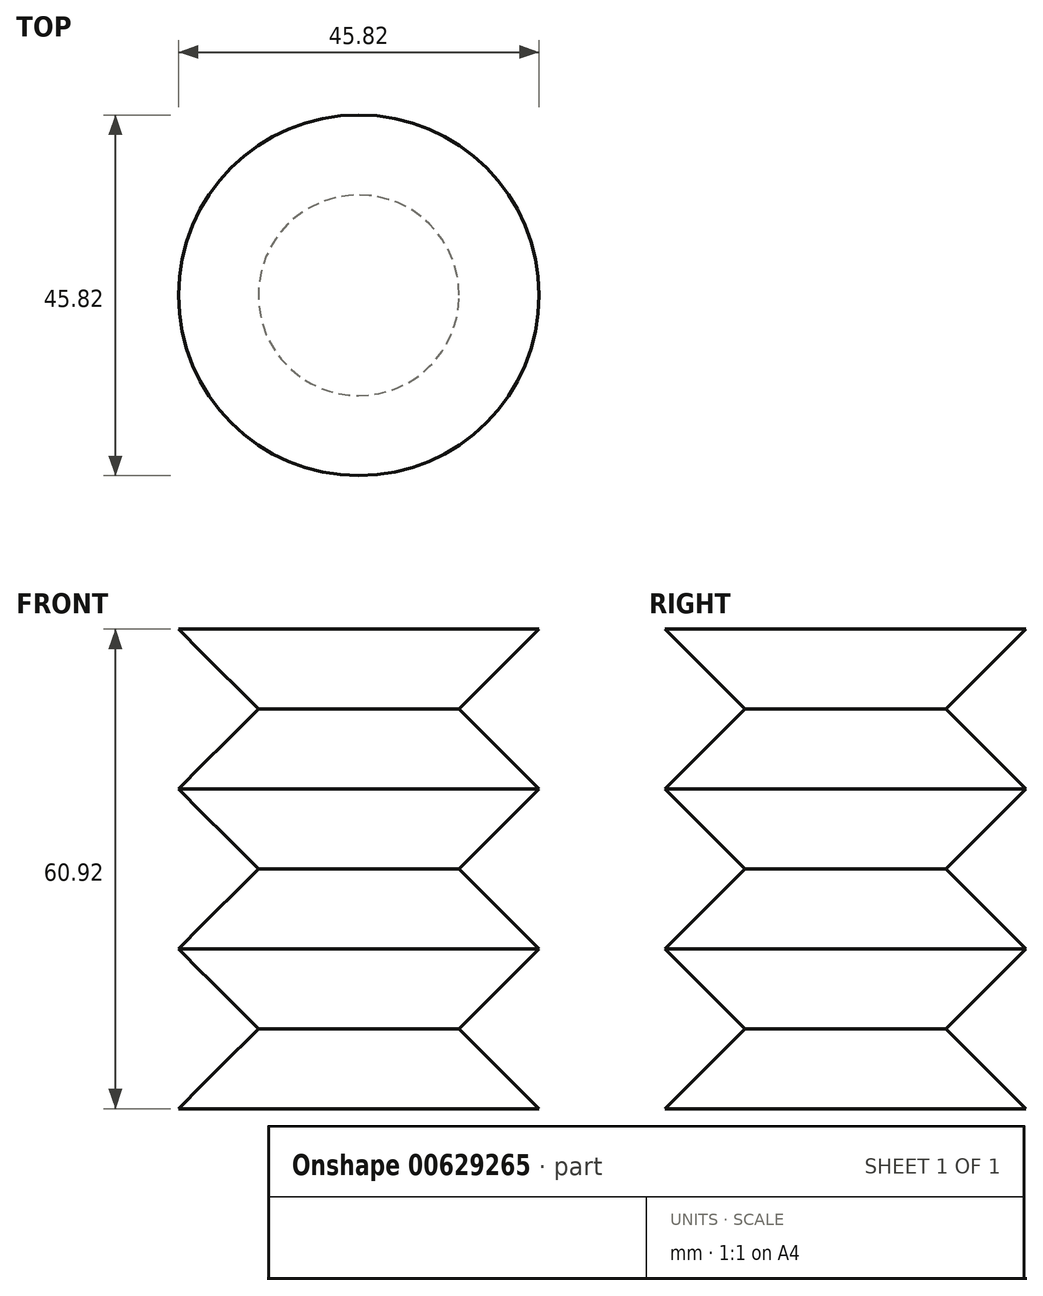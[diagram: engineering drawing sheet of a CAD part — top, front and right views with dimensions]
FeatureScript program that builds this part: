
annotation { "Feature Type Name" : "Feature", "Feature Type Description" : "" }
export const myFeature = defineFeature(function(context is Context, id is Id, definition is map)
    precondition{}
    {
        {
            var Q0;
            Q0=qCreatedBy(makeId("Front.planeOp"),FACE);
            var sketch = newSketch(context, id + "F0", { "sketchPlane" : qUnion([Q0])});
            skLineSegment(sketch, "E0", {"start": v(0, 30.46) * mm, "end": v(-22.9, 30.46) * mm});
            skLineSegment(sketch, "E1", {"start": v(-22.9, 30.46) * mm, "end": v(-12.75, 20.3) * mm});
            skLineSegment(sketch, "E2", {"start": v(-12.75, 20.3) * mm, "end": v(-22.9, 10.15) * mm});
            skLineSegment(sketch, "E3", {"start": v(-22.9, 10.15) * mm, "end": v(-12.75, 0) * mm});
            skLineSegment(sketch, "E4", {"start": v(-12.75, 0) * mm, "end": v(-22.9, -10.15) * mm});
            skLineSegment(sketch, "E5", {"start": v(-22.9, -10.15) * mm, "end": v(-12.75, -20.3) * mm});
            skLineSegment(sketch, "E6", {"start": v(-12.75, -20.3) * mm, "end": v(-22.9, -30.46) * mm});
            skLineSegment(sketch, "E7", {"start": v(-22.9, -30.46) * mm, "end": v(0, -30.46) * mm});
            skLineSegment(sketch, "E8", {"start": v(0, -30.46) * mm, "end": v(0, 30.46) * mm});
            skLineSegment(sketch, "E9", {"start": v(-12.75, 20.3) * mm, "end": v(-12.75, -20.3) * mm, "construction": true});
            skLineSegment(sketch, "E10", {"start": v(-22.9, 30.46) * mm, "end": v(-22.9, -30.46) * mm, "construction": true});
            skSolve(sketch);
        }
        {
            var Q0;
            Q0=makeQuery(id+"F0.imprint","IMPRINT",FACE,{"disambiguationData":[TD([[makeQuery(id+"F0.imprint","IMPRINT",EDGE,{"derivedFrom":sQuery(id+"F0.wireOp",EDGE,"E0")}),1.0]])]});
            var Q1;
            Q1=sQuery(id+"F0.wireOp",EDGE,"E8");
            revolve(context, id + "F1", {"surfaceOperationType" : NewSurfaceOperationType.NEW, "entities" : qUnion([Q0]), "axis" : qUnion([Q1]), "revolveType" : RevolveType.FULL});
        }
    });
